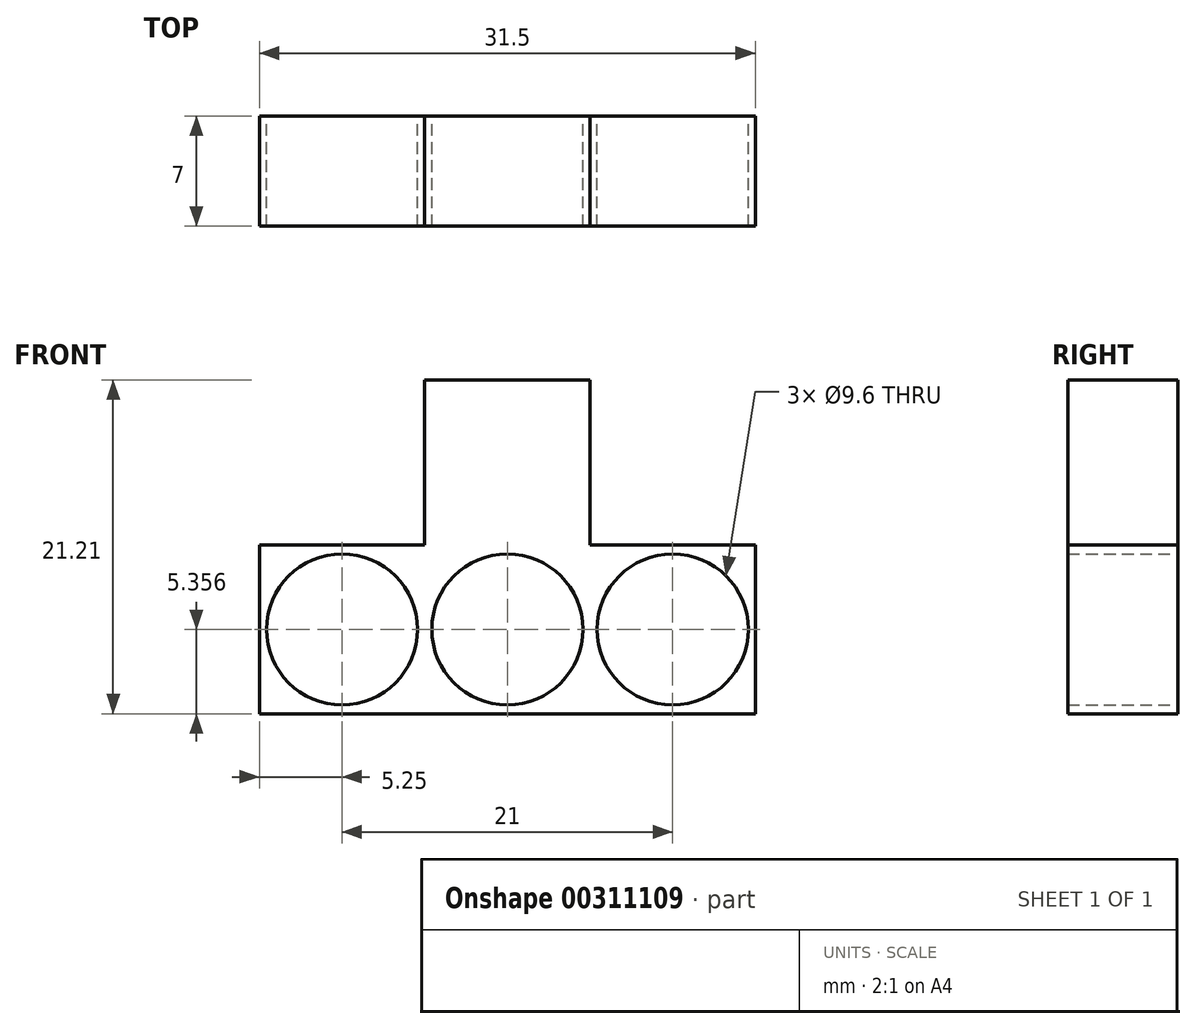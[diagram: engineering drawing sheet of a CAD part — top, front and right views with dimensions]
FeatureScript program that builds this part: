
annotation { "Feature Type Name" : "Feature", "Feature Type Description" : "" }
export const myFeature = defineFeature(function(context is Context, id is Id, definition is map)
    precondition{}
    {
        {
            var Q0;
            Q0=qCreatedBy(makeId("Front.planeOp"),FACE);
            var sketch = newSketch(context, id + "F0", { "sketchPlane" : qUnion([Q0])});
            skLineSegment(sketch, "E0.bottom", {"start": v(0, 0) * mm, "end": v(31.5, 0) * mm});
            skLineSegment(sketch, "E0.top", {"start": v(0, 10.71) * mm, "end": v(31.5, 10.71) * mm});
            skLineSegment(sketch, "E0.left", {"start": v(0, 0) * mm, "end": v(0, 10.71) * mm});
            skLineSegment(sketch, "E0.right", {"start": v(31.5, 0) * mm, "end": v(31.5, 10.71) * mm});
            skLineSegment(sketch, "E1", {"start": v(0, 5.36) * mm, "end": v(31.5, 5.36) * mm});
            skLineSegment(sketch, "E2", {"start": v(21, 10.71) * mm, "end": v(21, 0) * mm});
            skLineSegment(sketch, "E3", {"start": v(10.5, 10.71) * mm, "end": v(10.5, 0) * mm});
            skLineSegment(sketch, "E4", {"start": v(10.5, 10.71) * mm, "end": v(0, 0) * mm});
            skLineSegment(sketch, "E5", {"start": v(21, 10.71) * mm, "end": v(10.5, 0) * mm});
            skLineSegment(sketch, "E6", {"start": v(31.5, 10.71) * mm, "end": v(21, 0) * mm});
            skLineSegment(sketch, "E7", {"start": v(10.5, 10.71) * mm, "end": v(21, 0) * mm});
            skLineSegment(sketch, "E8", {"start": v(0, 10.71) * mm, "end": v(10.5, 0) * mm});
            skCircle(sketch, "E9", {"center": v(5.25, 5.36) * mm, "radius": 4.8 * mm});
            skCircle(sketch, "E10", {"center": v(15.75, 5.36) * mm, "radius": 4.8 * mm});
            skLineSegment(sketch, "E11", {"start": v(21, 10.71) * mm, "end": v(31.5, 0) * mm});
            skCircle(sketch, "E12", {"center": v(26.25, 5.36) * mm, "radius": 4.8 * mm});
            skLineSegment(sketch, "E13", {"start": v(10.5, 10.71) * mm, "end": v(10.5, 21.21) * mm});
            skLineSegment(sketch, "E14", {"start": v(21, 10.71) * mm, "end": v(21, 21.21) * mm});
            skLineSegment(sketch, "E15", {"start": v(10.5, 21.21) * mm, "end": v(21, 21.21) * mm});
            skSolve(sketch);
        }
        {
            var Q0;
            Q0 = qSketchRegion(id + "F0", true);
            extrude(context, id + "F1", {"entities" : qUnion([Q0]), "depth" : 7 * mm});
        }
    });
